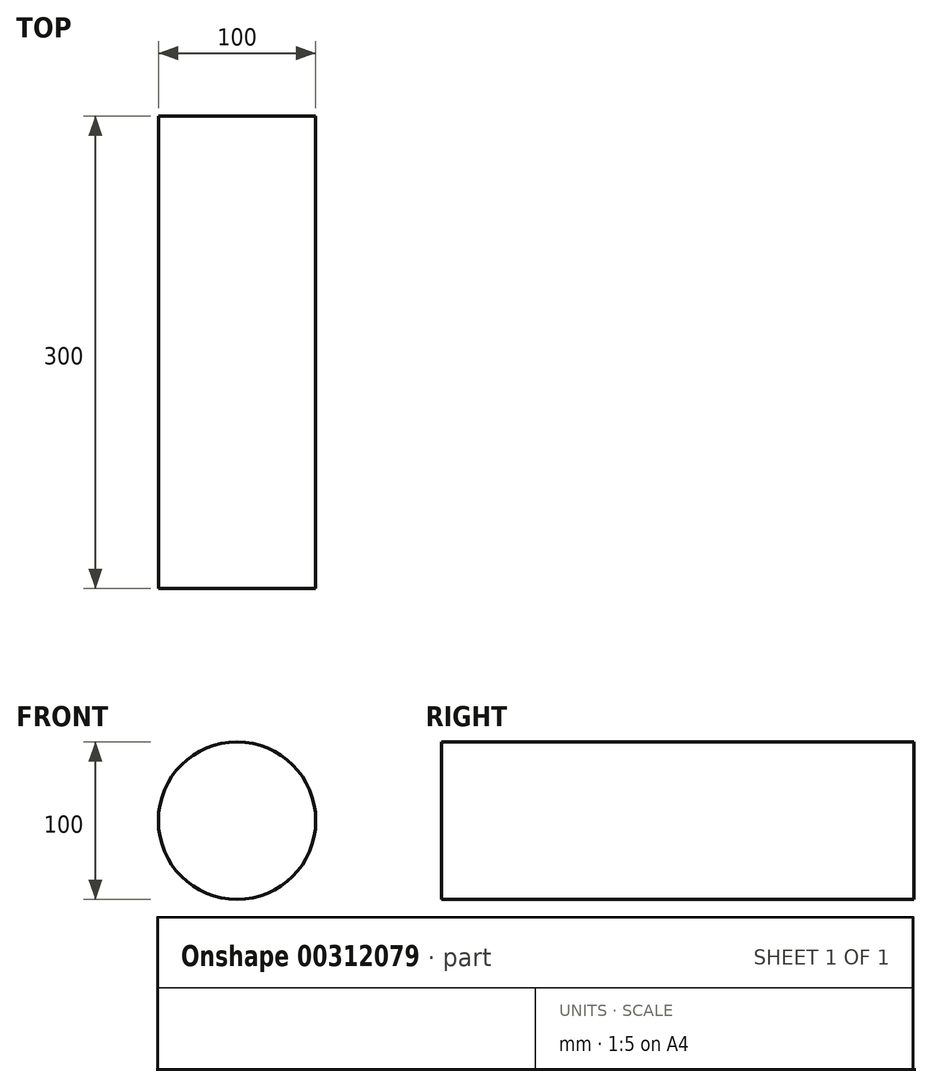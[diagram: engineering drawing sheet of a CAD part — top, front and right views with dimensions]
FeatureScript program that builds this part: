
annotation { "Feature Type Name" : "Feature", "Feature Type Description" : "" }
export const myFeature = defineFeature(function(context is Context, id is Id, definition is map)
    precondition{}
    {
        {
            var Q0;
            Q0=qCreatedBy(makeId("Front.planeOp"),FACE);
            var sketch = newSketch(context, id + "F0", { "sketchPlane" : qUnion([Q0])});
            skCircle(sketch, "E0", {"center": v(0, 0) * mm, "radius": 50 * mm});
            skSolve(sketch);
        }
        {
            var Q0;
            Q0 = qSketchRegion(id + "F0", true);
            extrude(context, id + "F1", {"entities" : qUnion([Q0]), "endBound" : BoundingType.SYMMETRIC, "depth" : 300 * mm});
        }
    });
